# Revit family: NLRS_52_PF_UN_AV_Aquaberg vloerput 4015146_BCB
name_source: partatom
category: Plumbing Fixtures
revit_build: Autodesk Revit 2017 (Build: 20160225_1515(x64)
units: mm (PartAtom-declared; Revit-internal decimal feet)

## family parameters
Always vertical = Yes
Cut with Voids When Loaded = Yes
OmniClass Number = 23.45.00.00
OmniClass Title = Sanitary, Laundry, and Cleaning Equipment
Part Type = Normal
Room Calculation Point = No
Round Connector Dimension = Use Radius
Shared = No
Work Plane-Based = No

## types (4) — shared parameters
Description = NLRS_C_omschrijving
IfcExportAs = IfcFlowTerminal
IfcExportType = IfcWasteTerminalType
Manufacturer = NLRS_C_merk
Model = NLRS_C_model
NLRS_C_aansluiting = onderaansluiting
NLRS_C_breedte = 146 mm  [stored 0.479003 ft]
NLRS_C_content_datum_gewijzigd = 2018-11
NLRS_C_content_datum_uitgifte = 2018-11
NLRS_C_content_versie = 1.0
NLRS_C_diameter = 50 mm  [stored 0.164042 ft]
NLRS_C_lengte = 146 mm  [stored 0.479003 ft]
NLRS_C_materiaal = NLRS_A_rvs
NLRS_C_materiaal_01 = NLRS_A_abs
NLRS_C_merk = Aquaberg
NLRS_C_model = 4015
NLRS_C_omschrijving = vloerput
NLRS_C_radius = 25 mm  [stored 0.082021 ft]
NLRS_C_revit_standaard = NLRS 2.5.2
NLRS_C_revit_versie = 2017
NLRS_C_serie = Aquaberg 4015
URL = https://www.aquaberg.nl

## type names (no varying parameters)
- 4015146
- 4015146A
- 4015146R
- 4015146RA

note: column(s) folded — value = type name in every type: NLRS_C_type

note: [stored X ft] marks values corroborated as IEEE doubles in the binary element streams (Revit-internal decimal feet)

## geometry (parser evidence)
native form markers: Sweep x2
no freeform markers — native parametric forms only
